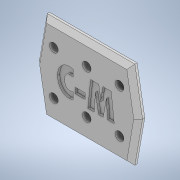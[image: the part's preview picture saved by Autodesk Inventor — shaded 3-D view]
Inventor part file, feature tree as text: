
AUTODESK INVENTOR PART (.ipt)
format: ipt  version: 2022 (Build 260153000, 153)  size: 192,512 bytes
history: native  units: in
note: dims shown in document units (in); Inventor stores cm internally (conversion verified against a paired STEP export)
features: extrude x2, sketch x2, chamfer x2
ambient origin geometry x8: Origin, YZ Plane, XZ Plane, XY Plane, X Axis, Y Axis, Z Axis, Center Point
bodies: Solid1 (feature_tree)
feature tree (6):
  extrude  "Extrusion1"  Depth=0.1181in
  sketch  "Sketch2"  dims[d11=0.0787in d12=0.0787in d13=45.0deg d20=0.7874in d21=105.0deg d22=0.0394in d23=0.0in d24=0.9252in d25=0.9252in d26=0.0787in d27=0.0787in d28=45.0deg]
  chamfer  "Chamfer1"  Distance=0.1181in
  extrude  "Extrusion2"  Depth=0.9252in TaperAngle=105.0deg
  chamfer  "Chamfer2"  Distance=0.0394in
  sketch  "Sketch1"  dims[d0=0.3937in d1=0.5906in d2=1.1811in d3=0.1575in d4=0.1575in d5=0.1575in d7=0.7874in d9=0.1181in d10=0.0in]
